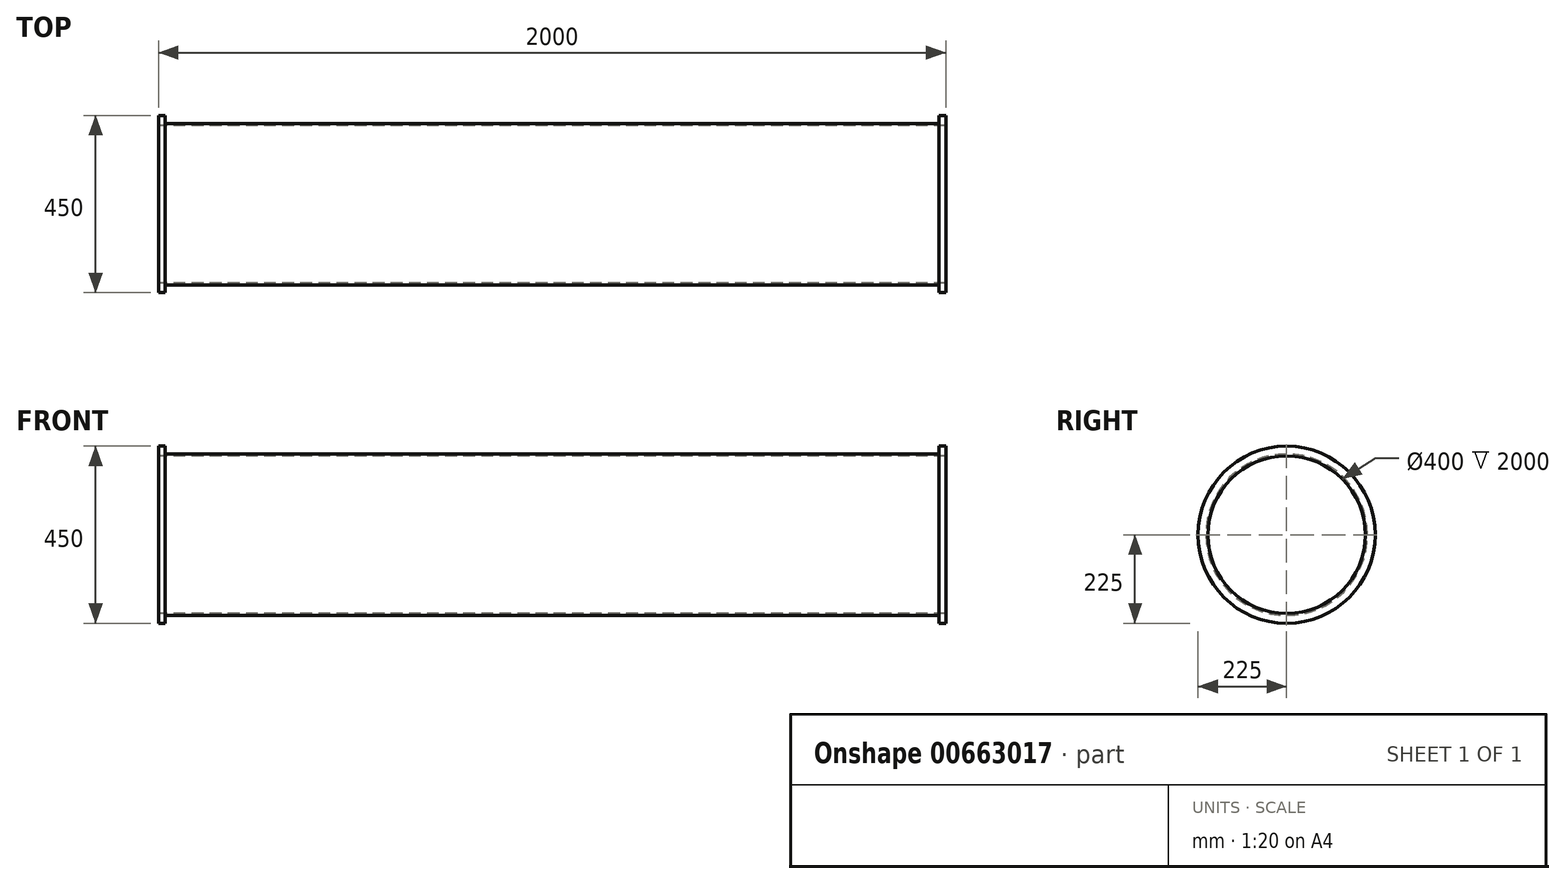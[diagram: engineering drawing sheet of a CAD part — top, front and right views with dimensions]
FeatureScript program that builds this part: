
annotation { "Feature Type Name" : "Feature", "Feature Type Description" : "" }
export const myFeature = defineFeature(function(context is Context, id is Id, definition is map)
    precondition{}
    {
        {
            var Q0;
            Q0=qCreatedBy(makeId("Front.planeOp"),FACE);
            var sketch = newSketch(context, id + "F0", { "sketchPlane" : qUnion([Q0])});
            skLineSegment(sketch, "E0", {"start": v(-750, 225) * mm, "end": v(-750, 200) * mm});
            skLineSegment(sketch, "E1", {"start": v(-750, 200) * mm, "end": v(1250, 200) * mm});
            skLineSegment(sketch, "E2", {"start": v(1250, 200) * mm, "end": v(1250, 225) * mm});
            skLineSegment(sketch, "E3", {"start": v(1250, 225) * mm, "end": v(1233, 225) * mm});
            skLineSegment(sketch, "E4", {"start": v(1233, 225) * mm, "end": v(1233, 205) * mm});
            skLineSegment(sketch, "E5", {"start": v(1233, 205) * mm, "end": v(-733, 205) * mm});
            skLineSegment(sketch, "E6", {"start": v(-733, 205) * mm, "end": v(-733, 225) * mm});
            skLineSegment(sketch, "E7", {"start": v(-733, 225) * mm, "end": v(-750, 225) * mm});
            skSolve(sketch);
        }
        {
            var Q0;
            Q0=qCreatedBy(makeId("Front.planeOp"),FACE);
            var sketch = newSketch(context, id + "F1", { "sketchPlane" : qUnion([Q0])});
            skLineSegment(sketch, "E8", {"start": v(-74.83, 0) * mm, "end": v(75.46, 0) * mm, "construction": true});
            skSolve(sketch);
        }
        {
            var Q0;
            Q0=makeQuery(id+"F0.imprint","IMPRINT",FACE,{"disambiguationData":[TD([[makeQuery(id+"F0.imprint","IMPRINT",EDGE,{"derivedFrom":sQuery(id+"F0.wireOp",EDGE,"E0")}),1.0]])]});
            var Q1;
            Q1=sQuery(id+"F1.wireOp",EDGE,"E8");
            revolve(context, id + "F2", {"entities" : qUnion([Q0]), "axis" : qUnion([Q1]), "revolveType" : RevolveType.FULL});
        }
    });
